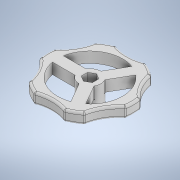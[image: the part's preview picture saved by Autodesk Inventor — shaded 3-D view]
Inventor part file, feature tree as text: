
AUTODESK INVENTOR PART (.ipt)
format: ipt  version: 2021 (Build 250183000, 183)  size: 331,264 bytes
history: native  units: mm
features: extrude x3, sketch x3, fillet x2
ambient origin geometry x8: Origin, YZ Plane, XZ Plane, XY Plane, X Axis, Y Axis, Z Axis, Center Point
bodies: Solid1 (feature_tree)
feature tree (8):
  extrude  "Extrusion1"  Depth=20.0mm
  extrude  "Extrusion2"  Depth=10.0mm
  fillet  "Fillet1"  Radius=10.0mm
  fillet  "Fillet2"  Radius=30.0mm
  extrude  "Extrusion3"  TaperAngle=120.0deg  [1 undecoded]
  sketch  "Sketch1"  dims[d0=7.5mm d1=20.0mm]
  sketch  "Sketch2"  dims[d2=20.0mm d3=0.0mm d5=60.0mm d8=10.0mm d9=30.0mm d11=360.0deg]
  sketch  "Sketch3"  dims[d15=40.0mm d16=120.0deg d17=1.745329mm d18=1.745329mm d20=2.0mm d21=60.0mm d23=360.0deg d25=10.0mm d26=0.0mm d27=2.0mm d28=1.0mm d29=6.0mm d30=20.0mm d31=0.0mm]
note: 1 required parameter value undecoded (feature->parameter linkage not recoverable at this tier; creation-order binding heuristic only, values carry confidence <= 0.55)
